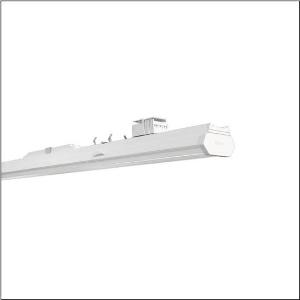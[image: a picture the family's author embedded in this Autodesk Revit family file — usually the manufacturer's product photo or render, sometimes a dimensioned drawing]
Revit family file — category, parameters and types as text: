
# Revit family: licross_11_protected_mo_51td11cn49xg
name_source: partatom
category: Lighting Fixtures
units: mm (PartAtom-declared; Revit-internal decimal feet)

## family parameters
Cut with Voids When Loaded = No
Host = Face
Light Source = No
Part Type = Normal
Room Calculation Point = No
Round Connector Dimension = Use Diameter
Shared = No

## types (1)
- --- (1 x LED, 9030 lm, 49.4 W, 4000K)
    Apparent Load = 49 VA
    CIE Flux Codes = 83 94 98 100 100
    Color Rendering = 80
    Color Temperature = 4000K
    Default Elevation = 1800 mm
    Description = Licross 11 Protected MO, luminaire insert, of sheet steel, galvanised, coil coated, white, length: 1.500mm, width: 90mm, height: 101mm, LED rated luminous flux: 9.030lm, light colour: 840, SDCM (Standard Deviation of Colour Matching)MacAdam ≤ 2 SDCM (initial), control gear: ON/OFF Multilumen, CLOi, with plug, 3-pole, with phase selection, mains connection: 220..240V, AC, 50/60Hz, start of lifetime: 49W, end of service life: 55W, internal wiring halogen-free, primary light control with lens, of plastic, primary optical cover: cover, of PMMA, light emission: direct distribution, primary light characteristic: symmetric, protection rating (complete): IP54, insulation class (complete): insulation class I (protective earthing), certification: CE, ENEC, VDE, UKCA, protection symbol: D if used in an environment with non-conductive dust loads with corresponding accessories, impact resistance: IK06, permissible ambient temperature for indoor applications: -35..+40°C, corresponds to IFS (International Featured Standards) requirements for safety and quality in the food industry, reducing of maximum allowable ambient temperature of 5°C with ceiling mounting, LABS conformity tested according to VDMA 24364:2018-05, The light source and the operating device comply with the requirements of the Ecodesign Regulation (EU) 2019/2020 and are replaceable in accordance with this regulation, packaging unit: 1 piece
    Height = 92 mm
    Lamp = 1 x LED
    Lamp Light Flux = 9030 lm
    Lamp Power = 49.4 W
    Lamp count = 1
    Length = 1500 mm
    Luminous efficacy = 183 lm/W
    Manufacturer = Siteco
    ModVariant = No
    Model = 51TD11CN49XG
    Mounting Place = Ceiling
    Mounting Type = Pendant
    Number of Poles = 1
    OnlyDefault = Yes
    Power Factor = 1
    Product Name = Licross 11 Protected MO
    Product group = luminaire insert | ceiling pendant
    ProductGroupID = 901
    Protection Class = Protection class I
    Protection Degree = IP 54
    RLX_Detail_Level = 1
    RLX_Emergency_Light_Flux = 0 lm
    RLX_Emergency_Type = 0
    RLX_Emergency_Type_DB = No
    RlxData = <blob elided: 22177 chars, md5=02618efd>
    Socket = socket
    Standby Power = 0 W
    System Light Flux = 9030 lm
    System Power = 49 W
    Type Comments = factory setting: luminous flux: 100 % | (A | C | E) | 113 mA
    Type Image = l_1256145.jpg
    URL = http://relux.com
    VarID = @adj_000681
    Voltage = 0 V
    Weight = 0.00 kg
    Width = 88 mm

## geometry (parser evidence)
native form markers: Blend x4, Sweep x10
no freeform markers — native parametric forms only
